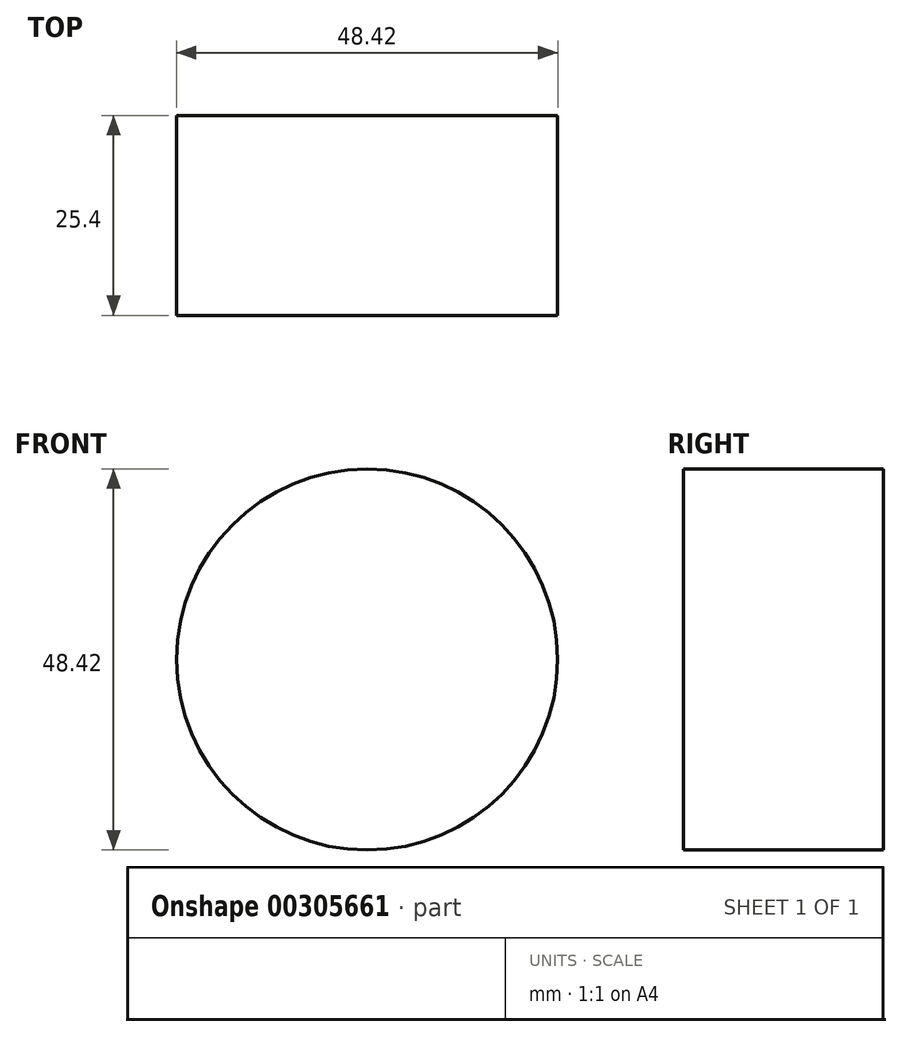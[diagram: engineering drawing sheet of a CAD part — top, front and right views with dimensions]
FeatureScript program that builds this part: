
annotation { "Feature Type Name" : "Feature", "Feature Type Description" : "" }
export const myFeature = defineFeature(function(context is Context, id is Id, definition is map)
    precondition{}
    {
        {
            var Q0;
            Q0=qCreatedBy(makeId("Front.planeOp"),FACE);
            var sketch = newSketch(context, id + "F0", { "sketchPlane" : qUnion([Q0])});
            skCircle(sketch, "E0", {"center": v(0, -3.71) * mm, "radius": 24.2 * mm});
            skSolve(sketch);
        }
        {
            var Q0;
            Q0=makeQuery(id+"F0.imprint","IMPRINT",FACE,{"disambiguationData":[TD([[makeQuery(id+"F0.imprint","IMPRINT",EDGE,{"derivedFrom":sQuery(id+"F0.wireOp",EDGE,"E0")}),1.0]])]});
            extrude(context, id + "F1", {"entities" : qUnion([Q0]), "depth" : 25.4 * mm});
        }
    });
